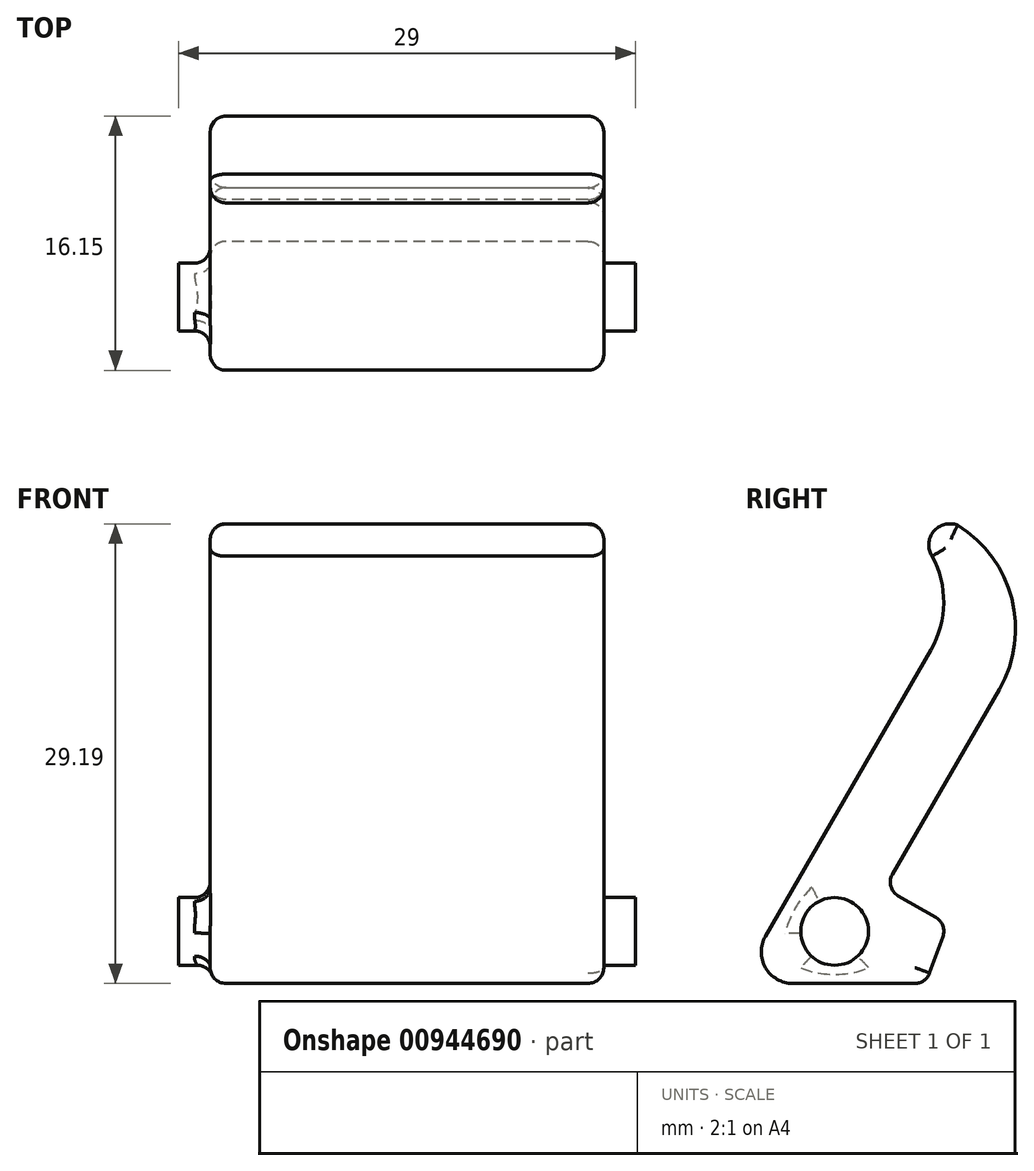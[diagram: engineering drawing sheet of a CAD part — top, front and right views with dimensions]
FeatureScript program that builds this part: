
annotation { "Feature Type Name" : "Feature", "Feature Type Description" : "" }
export const myFeature = defineFeature(function(context is Context, id is Id, definition is map)
    precondition{}
    {
        {
            var Q0;
            Q0=qCreatedBy(makeId("Right.planeOp"),FACE);
            var sketch = newSketch(context, id + "F0", { "sketchPlane" : qUnion([Q0])});
            skLineSegment(sketch, "E0", {"start": v(0, 0) * mm, "end": v(7.3, 0) * mm, "construction": true});
            skLineSegment(sketch, "E1", {"start": v(0, 0) * mm, "end": v(10, 17.32) * mm, "construction": true});
            skLineSegment(sketch, "E2", {"start": v(7.3, 0) * mm, "end": v(7.98, 1.88) * mm});
            skLineSegment(sketch, "E3", {"start": v(7.98, 1.88) * mm, "end": v(4.85, 3.69) * mm});
            skLineSegment(sketch, "E4", {"start": v(7.3, 0) * mm, "end": v(6.62, -1.88) * mm});
            skLineSegment(sketch, "E5", {"start": v(6.62, -1.88) * mm, "end": v(2, -1.88) * mm});
            skLineSegment(sketch, "E6", {"start": v(3.99, 4.19) * mm, "end": v(2, -1.88) * mm, "construction": true});
            skPoint(sketch, "E7", {"position": v(3, 1.15) * mm});
            skLineSegment(sketch, "E8", {"start": v(2, -1.88) * mm, "end": v(-1.84, -1.88) * mm, "construction": true});
            skPoint(sketch, "E9", {"position": v(0.82, 1.42) * mm});
            skCircle(sketch, "E10", {"center": v(0.82, 1.42) * mm, "radius": 2.15 * mm});
            skLineSegment(sketch, "E11", {"start": v(4.49, 5.05) * mm, "end": v(11.27, 16.8) * mm});
            skPoint(sketch, "E12.visualSharp", {"position": v(3.99, 4.19) * mm});
            skArc(sketch, "E12.filletArc", {"start": v(4.49, 5.05) * mm, "mid": v(4.39, 4.3) * mm, "end": v(4.85, 3.69) * mm});
            skLineSegment(sketch, "E13", {"start": v(6.94, 19.31) * mm, "end": v(-3.57, 1.12) * mm});
            skLineSegment(sketch, "E14", {"start": v(2, -1.88) * mm, "end": v(-1.84, -1.88) * mm});
            skPoint(sketch, "E15.newPointA", {"position": v(-1.84, -1.88) * mm});
            skArc(sketch, "E15.filletArc", {"start": v(-3.57, 1.12) * mm, "mid": v(-3.57, -0.88) * mm, "end": v(-1.84, -1.88) * mm});
            skLineSegment(sketch, "E16", {"start": v(-3.84, -5.18) * mm, "end": v(-3.84, 20.27) * mm, "construction": true});
            skLineSegment(sketch, "E17", {"start": v(11.27, 16.8) * mm, "end": v(-1.69, 24.3) * mm, "construction": true});
            skArc(sketch, "E18", {"start": v(11.27, 16.8) * mm, "mid": v(12.07, 22.55) * mm, "end": v(8.63, 27.22) * mm});
            skArc(sketch, "E19", {"start": v(6.94, 19.31) * mm, "mid": v(7.75, 22.27) * mm, "end": v(7, 25.26) * mm});
            skArc(sketch, "E20", {"start": v(8.63, 27.22) * mm, "mid": v(7.1, 26.82) * mm, "end": v(7, 25.26) * mm});
            skSolve(sketch);
        }
        {
            var Q0;
            Q0=makeQuery(id+"F0.imprint","IMPRINT",FACE,{"disambiguationData":[TD([[makeQuery(id+"F0.imprint","IMPRINT",EDGE,{"derivedFrom":sQuery(id+"F0.wireOp",EDGE,"E10")}),1.0]])]});
            extrude(context, id + "F1", {"entities" : qUnion([Q0]), "endBound" : BoundingType.SYMMETRIC, "depth" : 29 * mm, "offsetDistance" : 25 * mm});
        }
        {
            var Q0;
            Q0 = qSketchRegion(id + "F0", true);
            extrude(context, id + "F2", {"entities" : qUnion([Q0]), "operationType" : NewBodyOperationType.ADD, "endBound" : BoundingType.SYMMETRIC, "depth" : 25 * mm, "offsetDistance" : 25 * mm});
        }
        {
            var Q0;
            Q0=makeQuery(id+"F2.opExtrude","CAP_EDGE",EDGE,{"disambiguationData":[OSD([sQuery(id+"F0.wireOp",EDGE,"E18")])],"isStart":true});
            var Q1;
            Q1=makeQuery(id+"F2.opExtrude","CAP_EDGE",EDGE,{"disambiguationData":[OSD([sQuery(id+"F0.wireOp",EDGE,"E11")])],"isStart":true});
            var Q2;
            Q2=makeQuery(id+"F2.opExtrude","CAP_EDGE",EDGE,{"disambiguationData":[OSD([sQuery(id+"F0.wireOp",EDGE,"E3")])],"isStart":true});
            var Q3;
            Q3=makeQuery(id+"F2.opExtrude","CAP_EDGE",EDGE,{"disambiguationData":[OSD([sQuery(id+"F0.wireOp",EDGE,"E12.filletArc")])],"isStart":true});
            var Q4;
            Q4=makeQuery(id+"F2.opExtrude","CAP_EDGE",EDGE,{"disambiguationData":[OSD([sQuery(id+"F0.wireOp",EDGE,"E2"),sQuery(id+"F0.wireOp",EDGE,"E4")])],"isStart":true});
            var Q5;
            Q5=makeQuery(id+"F2.opExtrude","CAP_EDGE",EDGE,{"disambiguationData":[OSD([sQuery(id+"F0.wireOp",EDGE,"E5"),sQuery(id+"F0.wireOp",EDGE,"E14")])],"isStart":true});
            var Q6;
            Q6=makeQuery(id+"F2.opExtrude","CAP_EDGE",EDGE,{"disambiguationData":[OSD([sQuery(id+"F0.wireOp",EDGE,"E15.filletArc")])],"isStart":true});
            var Q7;
            Q7=makeQuery(id+"F2.opExtrude","CAP_EDGE",EDGE,{"disambiguationData":[OSD([sQuery(id+"F0.wireOp",EDGE,"E13")])],"isStart":true});
            var Q8;
            Q8=makeQuery(id+"F2.opExtrude","CAP_EDGE",EDGE,{"disambiguationData":[OSD([sQuery(id+"F0.wireOp",EDGE,"E19")])],"isStart":true});
            var Q9;
            Q9=makeQuery(id+"F2.opExtrude","CAP_EDGE",EDGE,{"disambiguationData":[OSD([sQuery(id+"F0.wireOp",EDGE,"E20")])],"isStart":true});
            var Q10;
            Q10=makeQuery(id+"F2.opExtrude","SWEPT_EDGE",EDGE,{"disambiguationData":[OSD([sQuery(id+"F0.wireOp",EDGE,"E4"),sQuery(id+"F0.wireOp",EDGE,"E5")])]});
            var Q11;
            Q11=makeQuery(id+"F2.opExtrude","SWEPT_EDGE",EDGE,{"disambiguationData":[OSD([sQuery(id+"F0.wireOp",EDGE,"E2"),sQuery(id+"F0.wireOp",EDGE,"E3")])]});
            var Q12;
            Q12=makeQuery(id+"F2.opExtrude","CAP_EDGE",EDGE,{"disambiguationData":[OSD([sQuery(id+"F0.wireOp",EDGE,"E2"),sQuery(id+"F0.wireOp",EDGE,"E4")])],"isStart":false});
            var Q13;
            Q13=makeQuery(id+"F2.opExtrude","CAP_EDGE",EDGE,{"disambiguationData":[OSD([sQuery(id+"F0.wireOp",EDGE,"E3")])],"isStart":false});
            var Q14;
            Q14=makeQuery(id+"F2.opExtrude","CAP_EDGE",EDGE,{"disambiguationData":[OSD([sQuery(id+"F0.wireOp",EDGE,"E12.filletArc")])],"isStart":false});
            var Q15;
            Q15=makeQuery(id+"F2.opExtrude","CAP_EDGE",EDGE,{"disambiguationData":[OSD([sQuery(id+"F0.wireOp",EDGE,"E11")])],"isStart":false});
            var Q16;
            Q16=makeQuery(id+"F2.opExtrude","CAP_EDGE",EDGE,{"disambiguationData":[OSD([sQuery(id+"F0.wireOp",EDGE,"E18")])],"isStart":false});
            var Q17;
            Q17=makeQuery(id+"F2.opExtrude","CAP_EDGE",EDGE,{"disambiguationData":[OSD([sQuery(id+"F0.wireOp",EDGE,"E19")])],"isStart":false});
            var Q18;
            Q18=makeQuery(id+"F2.opExtrude","CAP_EDGE",EDGE,{"disambiguationData":[OSD([sQuery(id+"F0.wireOp",EDGE,"E20")])],"isStart":false});
            var Q19;
            Q19=makeQuery(id+"F2.opExtrude","CAP_EDGE",EDGE,{"disambiguationData":[OSD([sQuery(id+"F0.wireOp",EDGE,"E13")])],"isStart":false});
            var Q20;
            Q20=makeQuery(id+"F2.opExtrude","CAP_EDGE",EDGE,{"disambiguationData":[OSD([sQuery(id+"F0.wireOp",EDGE,"E5"),sQuery(id+"F0.wireOp",EDGE,"E14")])],"isStart":false});
            var Q21;
            Q21=makeQuery(id+"F2.opExtrude","CAP_EDGE",EDGE,{"disambiguationData":[OSD([sQuery(id+"F0.wireOp",EDGE,"E15.filletArc")])],"isStart":false});
            fillet(context, id + "F3", {"entities" : qUnion([Q0, Q1, Q2, Q3, Q4, Q5, Q6, Q7, Q8, Q9, Q10, Q11, Q12, Q13, Q14, Q15, Q16, Q17, Q18, Q19, Q20, Q21]), "radius" : 1 * mm, "tangentPropagation" : true, "allowEdgeOverflow" : false});
        }
        {
            var Q0;
            Q0=makeQuery(id+"F2.opExtrude","CAP_EDGE",EDGE,{"disambiguationData":[OSD([sQuery(id+"F0.wireOp",EDGE,"E10")])],"isStart":true});
            var Q1;
            Q1=makeQuery(id+"F2.opExtrude","CAP_EDGE",EDGE,{"disambiguationData":[OSD([sQuery(id+"F0.wireOp",EDGE,"E10")])],"isStart":false});
            fillet(context, id + "F4", {"entities" : qUnion([Q0, Q1]), "radius" : 1 * mm, "tangentPropagation" : true, "allowEdgeOverflow" : false});
        }
    });
